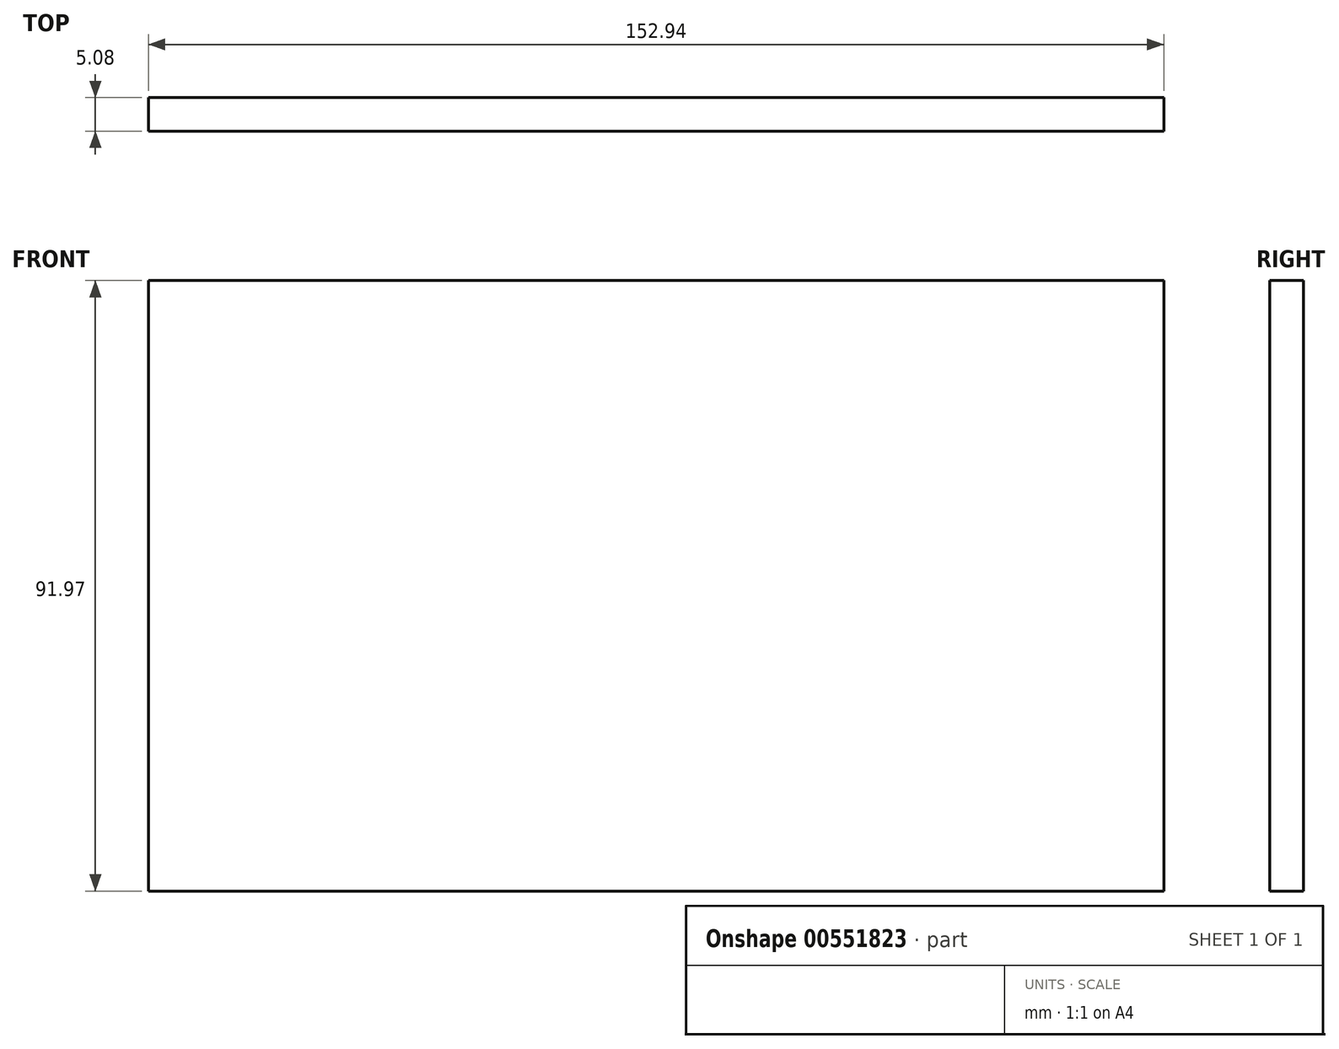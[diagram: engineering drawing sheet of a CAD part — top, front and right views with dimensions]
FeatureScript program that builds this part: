
annotation { "Feature Type Name" : "Feature", "Feature Type Description" : "" }
export const myFeature = defineFeature(function(context is Context, id is Id, definition is map)
    precondition{}
    {
        {
            var Q0;
            Q0=qCreatedBy(makeId("Front.planeOp"),FACE);
            var sketch = newSketch(context, id + "F0", { "sketchPlane" : qUnion([Q0])});
            skLineSegment(sketch, "E0.bottom", {"start": v(-76.47, 45.62) * mm, "end": v(76.47, 45.62) * mm});
            skLineSegment(sketch, "E0.top", {"start": v(-76.47, -46.35) * mm, "end": v(76.47, -46.35) * mm});
            skLineSegment(sketch, "E0.left", {"start": v(-76.47, 45.62) * mm, "end": v(-76.47, -46.35) * mm});
            skLineSegment(sketch, "E0.right", {"start": v(76.47, 45.62) * mm, "end": v(76.47, -46.35) * mm});
            skSolve(sketch);
        }
        {
            var Q0;
            Q0 = qSketchRegion(id + "F0", true);
            extrude(context, id + "F1", {"entities" : qUnion([Q0]), "depth" : 5.08 * mm, "offsetDistance" : 25.4 * mm});
        }
    });
